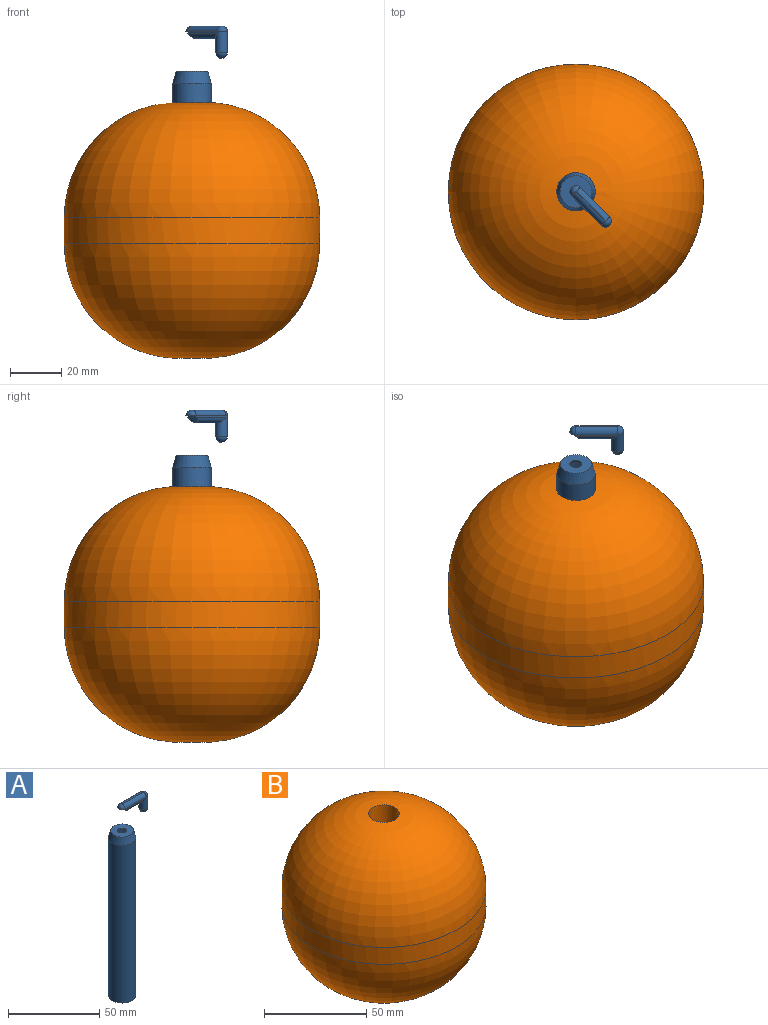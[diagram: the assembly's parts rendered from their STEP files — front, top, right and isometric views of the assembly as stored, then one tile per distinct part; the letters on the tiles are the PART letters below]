
ASSEMBLY  parts=2 mates=1
PART A: 19 faces, bbox 35.6x24.4x137.4 mm
  f0: cylinder r=2.35mm len=15.49mm, axis (0,0,-1), area 0mm2, adj f1,f2,f3,f4
  f1: plane 21.88x21.88mm, normal (0,0,-1), area 104.5mm2, adj f0,f5
  f2: plane 16.33x0.51mm, normal (0,1,0), area 8.3mm2, adj f0,f6,f7,f8
  f3: torus R=0.07mm, axis (0,0,1), area 17.2mm2, adj f0,f4,f8,f9,f10
  f4: cylinder r=2.35mm len=4.71mm, axis (0,0,-1), area 12.7mm2, adj f0,f3,f6,f11,f12,f13
  f5: cone r=6.23mm half-angle=15deg, axis (0,0,-1), area 211.7mm2, adj f1,f14
  f6: cylinder r=2.29mm len=16.33mm, axis (1,0,0), area 50.2mm2, adj f2,f4,f7,f11
  f7: cylinder r=2.36mm len=8.13mm, axis (0,0,-1), area 105.8mm2, adj f2,f6,f11,f12,f13,f15,f16
  f8: cylinder r=2.29mm len=16.33mm, axis (-1,0,0), area 58.6mm2, adj f2,f3,f9,f16
  f9: plane 16.47x0.15mm, normal (0,0,-1), area 2.3mm2, adj f3,f8,f10,f16
  f10: cylinder r=2.29mm len=16.33mm, axis (1,0,0), area 58.6mm2, adj f3,f9,f13,f16
  f11: plane 11.62x0.14mm, normal (0,0,1), area 1.6mm2, adj f4,f6,f7,f12
  f12: cylinder r=2.29mm len=16.33mm, axis (-1,0,0), area 50.2mm2, adj f4,f7,f11,f13
  f13: plane 25.75x9.93mm, normal (0,-1,0), area 8.3mm2, adj f4,f7,f10,f12
  f14: cylinder r=7.5mm len=105.5mm, axis (0,0,-1), area 4971.4mm2, adj f5,f17
  f15: torus R=0.07mm, axis (0,0,1), area 34.5mm2, adj f7,f18
  f16: torus R=0.07mm, axis (0,0,1), area 17.2mm2, adj f7,f8,f9,f10
  f17: plane 15x15mm, normal (0,0,1), area 176.7mm2, adj f14
  f18: plane 0.15x0.15mm, normal (0,0,1), area 0mm2, adj f15
PART B: 4 faces, bbox 100x100x100 mm
  f0: cylinder r=7.5mm len=100mm, axis (0,0,-1), area 4712.4mm2, adj f2,f3
  f1: cylinder r=50mm len=100mm, axis (0,0,-1), area 3185.3mm2, adj f2,f3
  f2: torus R=5mm, axis (0,0,-1), area 14845.9mm2, adj f0,f1
  f3: torus R=5mm, axis (0,0,1), area 14845.9mm2, adj f0,f1
PLACE A rot(axis=(0,0,-1),45deg) t=(-7.66,-31.25,-0.04)mm
PLACE B t=(-7.66,-31.25,-2.03)mm
MATE cylindrical A.f0 <-> B.f0  axis (0,0,1) through (-7.66,-31.25,60.16)mm
